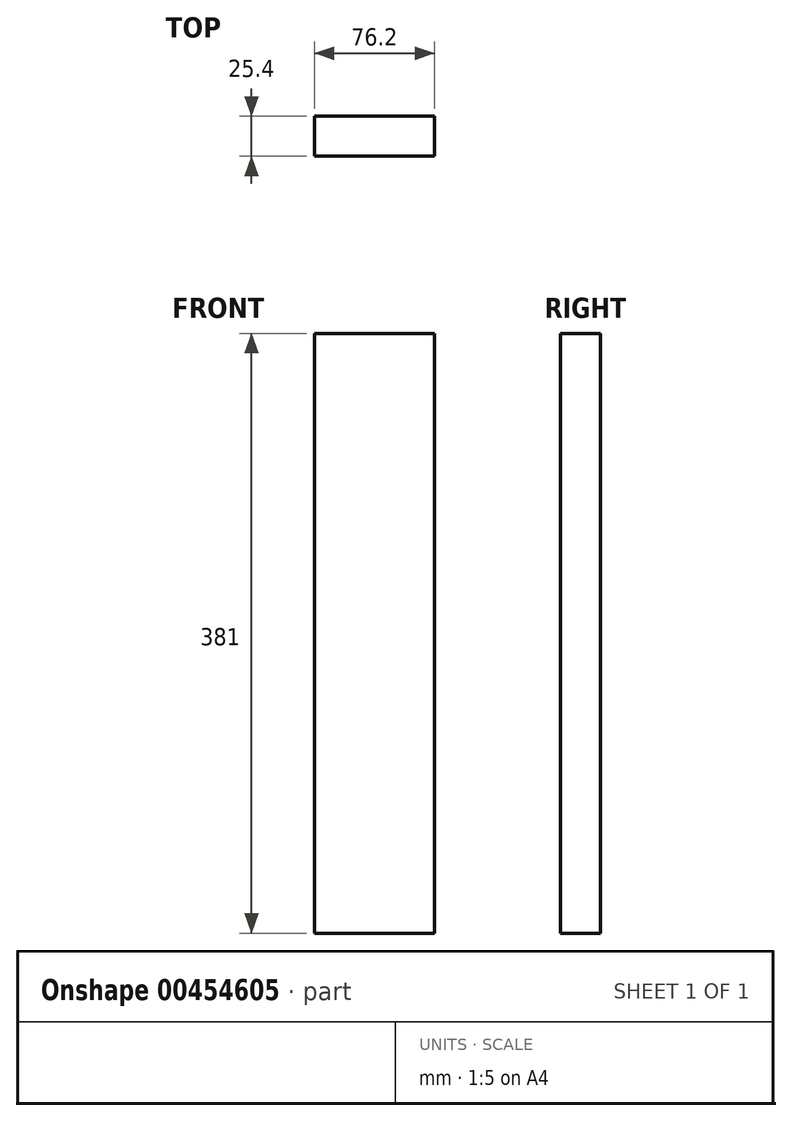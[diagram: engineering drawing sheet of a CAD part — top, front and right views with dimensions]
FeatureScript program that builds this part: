
annotation { "Feature Type Name" : "Feature", "Feature Type Description" : "" }
export const myFeature = defineFeature(function(context is Context, id is Id, definition is map)
    precondition{}
    {
        {
            var Q0;
            Q0=qCreatedBy(makeId("Top.planeOp"),FACE);
            var sketch = newSketch(context, id + "F0", { "sketchPlane" : qUnion([Q0])});
            skLineSegment(sketch, "E0.bottom", {"start": v(38.1, 12.7) * mm, "end": v(-38.1, 12.7) * mm});
            skLineSegment(sketch, "E0.top", {"start": v(38.1, -12.7) * mm, "end": v(-38.1, -12.7) * mm});
            skLineSegment(sketch, "E0.left", {"start": v(38.1, 12.7) * mm, "end": v(38.1, -12.7) * mm});
            skLineSegment(sketch, "E0.right", {"start": v(-38.1, 12.7) * mm, "end": v(-38.1, -12.7) * mm});
            skPoint(sketch, "E0.middle", {"position": v(0, 0) * mm});
            skSolve(sketch);
        }
        {
            var Q0;
            Q0=makeQuery(id+"F0.imprint","IMPRINT",FACE,{"disambiguationData":[TD([[makeQuery(id+"F0.imprint","IMPRINT",EDGE,{"derivedFrom":sQuery(id+"F0.wireOp",EDGE,"E0.bottom")}),1.0]])]});
            extrude(context, id + "F1", {"entities" : qUnion([Q0]), "depth" : 381 * mm});
        }
    });
